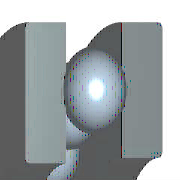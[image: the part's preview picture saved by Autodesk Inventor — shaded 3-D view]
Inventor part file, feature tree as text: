
AUTODESK INVENTOR PART (.ipt)
format: ipt  version: 2022 (Build 260153000, 153)  size: 370,688 bytes
history: native  units: mm (DEFAULTED — no unit token found)
features: sketch x1, other x1, pattern_circular x1
ambient origin geometry x8: Origin, YZ Plane, XZ Plane, XY Plane, X Axis, Y Axis, Z Axis, Center Point
bodies: Solid1 (feature_tree), Body (feature_tree)
feature tree (3):
  sketch  "Sketch"  dims[d0=1.4mm d9=90.0deg d10=90.0deg d1=320.0mm d2=360.0deg d3=3.08mm d4=0.3mm d5=0.3mm d6=0.0mm d7=0.0mm d8=55.0mm d11=55.0mm d12=62.5mm d13=70.0mm d14=70.0mm d15=3.5mm d16=7.0mm d18=2.1mm d19=0.0mm d46=0.0mm d47=0.0mm]
  other  "Ball"
  pattern_circular  "Balls"  Angle=90.0deg  [1 undecoded]
note: 1 required parameter value undecoded (feature->parameter linkage not recoverable at this tier; creation-order binding heuristic only, values carry confidence <= 0.55)
